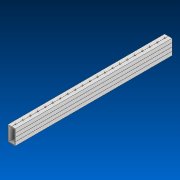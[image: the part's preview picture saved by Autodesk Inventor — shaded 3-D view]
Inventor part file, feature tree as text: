
AUTODESK INVENTOR PART (.ipt)
format: ipt  version: 2022.2 (Build 262287000, 287)  size: 482,304 bytes
history: native  units: in
note: dims shown in document units (in); Inventor stores cm internally (conversion verified against a paired STEP export)
features: other x22, extrude x1, pattern_linear x1, sketch x1
ambient origin geometry x8: Origin, YZ Plane, XZ Plane, XY Plane, X Axis, Y Axis, Z Axis, Center Point
bodies: Solid1 (feature_tree)
feature tree (25):
  extrude  "Extrusion1"  Depth=2.0in
  other  "Work Axis1"
  pattern_linear  "Rectangular Pattern1"  Spacing1=38.0in  [1 undecoded]
  sketch  "Sketch1"  dims[d0=1.0in d1=2.0in d2=38.0in d3=0.0in d4=8.2677in d6=1.0in]
  other  "Work Axis2"
  other  "Work Axis3"
  other  "Work Axis4"
  other  "Work Axis5"
  other  "Work Axis6"
  other  "Work Axis7"
  other  "Work Axis8"
  other  "Work Axis9"
  other  "Work Axis10"
  other  "Work Axis60"
  other  "Work Axis61"
  other  "Work Axis62"
  other  "Work Axis63"
  other  "Work Axis64"
  other  "Work Axis65"
  other  "Work Axis66"
  other  "Work Axis67"
  other  "Work Axis68"
  other  "Work Axis69"
  other  "Work Axis70"
  other  "Cut-Extrude2"
note: 1 required parameter value undecoded (feature->parameter linkage not recoverable at this tier; creation-order binding heuristic only, values carry confidence <= 0.55)
